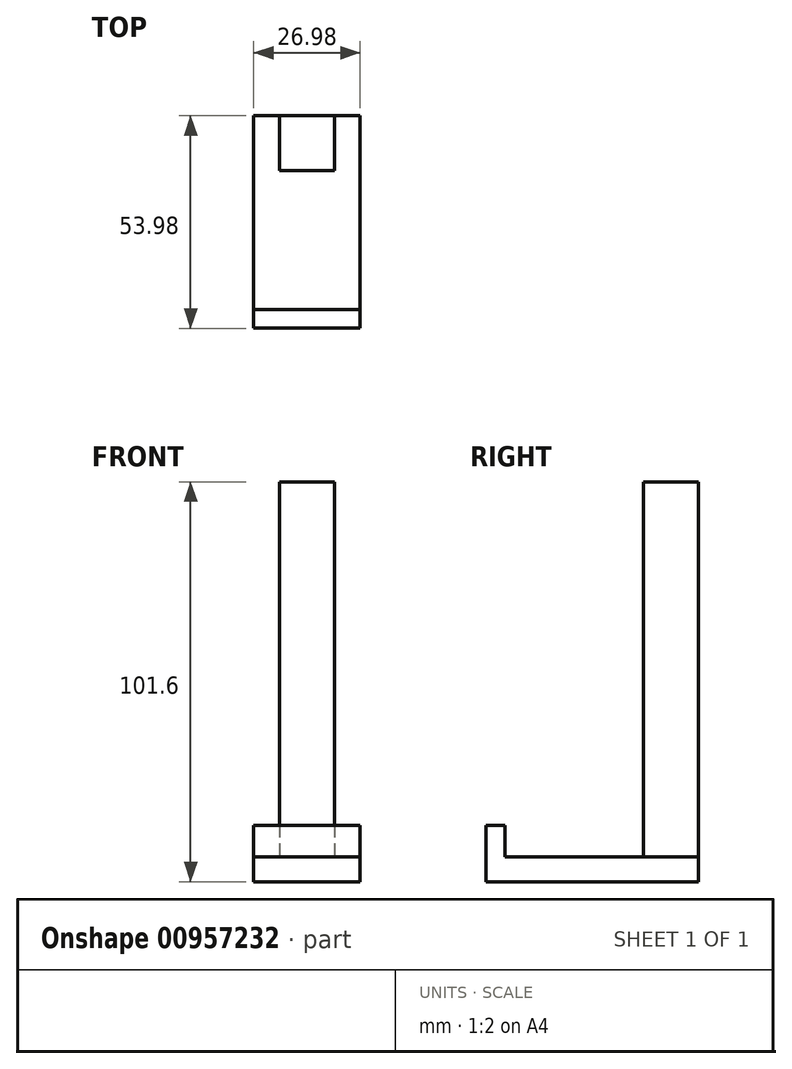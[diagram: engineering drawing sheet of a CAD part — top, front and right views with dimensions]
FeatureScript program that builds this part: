
annotation { "Feature Type Name" : "Feature", "Feature Type Description" : "" }
export const myFeature = defineFeature(function(context is Context, id is Id, definition is map)
    precondition{}
    {
        {
            var Q0;
            Q0=qCreatedBy(makeId("Top.planeOp"),FACE);
            var sketch = newSketch(context, id + "F0", { "sketchPlane" : qUnion([Q0])});
            skLineSegment(sketch, "E0.bottom", {"start": v(-27.18, 11.52) * mm, "end": v(-0.2, 11.52) * mm});
            skLineSegment(sketch, "E0.top", {"start": v(-27.18, -42.46) * mm, "end": v(-0.2, -42.46) * mm});
            skLineSegment(sketch, "E0.left", {"start": v(-27.18, 11.52) * mm, "end": v(-27.18, -42.46) * mm});
            skLineSegment(sketch, "E0.right", {"start": v(-0.2, 11.52) * mm, "end": v(-0.2, -42.46) * mm});
            skSolve(sketch);
        }
        {
            var Q0;
            Q0=makeQuery(id+"F0.imprint","IMPRINT",FACE,{"disambiguationData":[TD([[makeQuery(id+"F0.imprint","IMPRINT",EDGE,{"derivedFrom":sQuery(id+"F0.wireOp",EDGE,"E0.bottom")}),-1.0]])]});
            extrude(context, id + "F1", {"entities" : qUnion([Q0]), "depth" : 6.35 * mm, "offsetDistance" : 25.4 * mm});
        }
        {
            var Q0;
            Q0=makeQuery(id+"F1.opExtrude","CAP_FACE",FACE,{"disambiguationData":[OSD([sQuery(id+"F0.wireOp",EDGE,"E0.bottom"),sQuery(id+"F0.wireOp",EDGE,"E0.top"),sQuery(id+"F0.wireOp",EDGE,"E0.left"),sQuery(id+"F0.wireOp",EDGE,"E0.right")])],"isStart":false});
            var sketch = newSketch(context, id + "F2", { "sketchPlane" : qUnion([Q0])});
            skLineSegment(sketch, "E1.bottom", {"start": v(-27.18, -37.64) * mm, "end": v(-0.2, -37.64) * mm});
            skLineSegment(sketch, "E1.top", {"start": v(-27.18, -42.4) * mm, "end": v(-0.2, -42.4) * mm});
            skLineSegment(sketch, "E1.left", {"start": v(-27.18, -37.64) * mm, "end": v(-27.18, -42.4) * mm});
            skLineSegment(sketch, "E1.right", {"start": v(-0.2, -37.64) * mm, "end": v(-0.2, -42.4) * mm});
            skSolve(sketch);
        }
        {
            var Q0;
            Q0 = qSketchRegion(id + "F2", true);
            extrude(context, id + "F3", {"entities" : qUnion([Q0]), "operationType" : NewBodyOperationType.ADD, "depth" : 7.94 * mm, "offsetDistance" : 25.4 * mm});
        }
        {
            var Q0;
            Q0=qCreatedBy(makeId("Top.planeOp"),FACE);
            var sketch = newSketch(context, id + "F4", { "sketchPlane" : qUnion([Q0])});
            skLineSegment(sketch, "E2.bottom", {"start": v(-20.67, 11.52) * mm, "end": v(-6.7, 11.52) * mm});
            skLineSegment(sketch, "E2.top", {"start": v(-20.67, -2.45) * mm, "end": v(-6.7, -2.45) * mm});
            skLineSegment(sketch, "E2.left", {"start": v(-20.67, 11.52) * mm, "end": v(-20.67, -2.45) * mm});
            skLineSegment(sketch, "E2.right", {"start": v(-6.7, 11.52) * mm, "end": v(-6.7, -2.45) * mm});
            skLineSegment(sketch, "E3", {"start": v(-13.69, -2.45) * mm, "end": v(-13.69, 11.52) * mm});
            skSolve(sketch);
        }
        {
            var Q0;
            Q0=makeQuery(id+"F4.imprint","IMPRINT",FACE,{"disambiguationData":[TD([[makeQuery(id+"F4.imprint","IMPRINT",EDGE,{"derivedFrom":sQuery(id+"F4.wireOp",EDGE,"E2.bottom")}),-1.0]])]});
            extrude(context, id + "F5", {"entities" : qUnion([Q0]), "operationType" : NewBodyOperationType.ADD, "depth" : 101.6 * mm, "offsetDistance" : 25.4 * mm});
        }
    });
